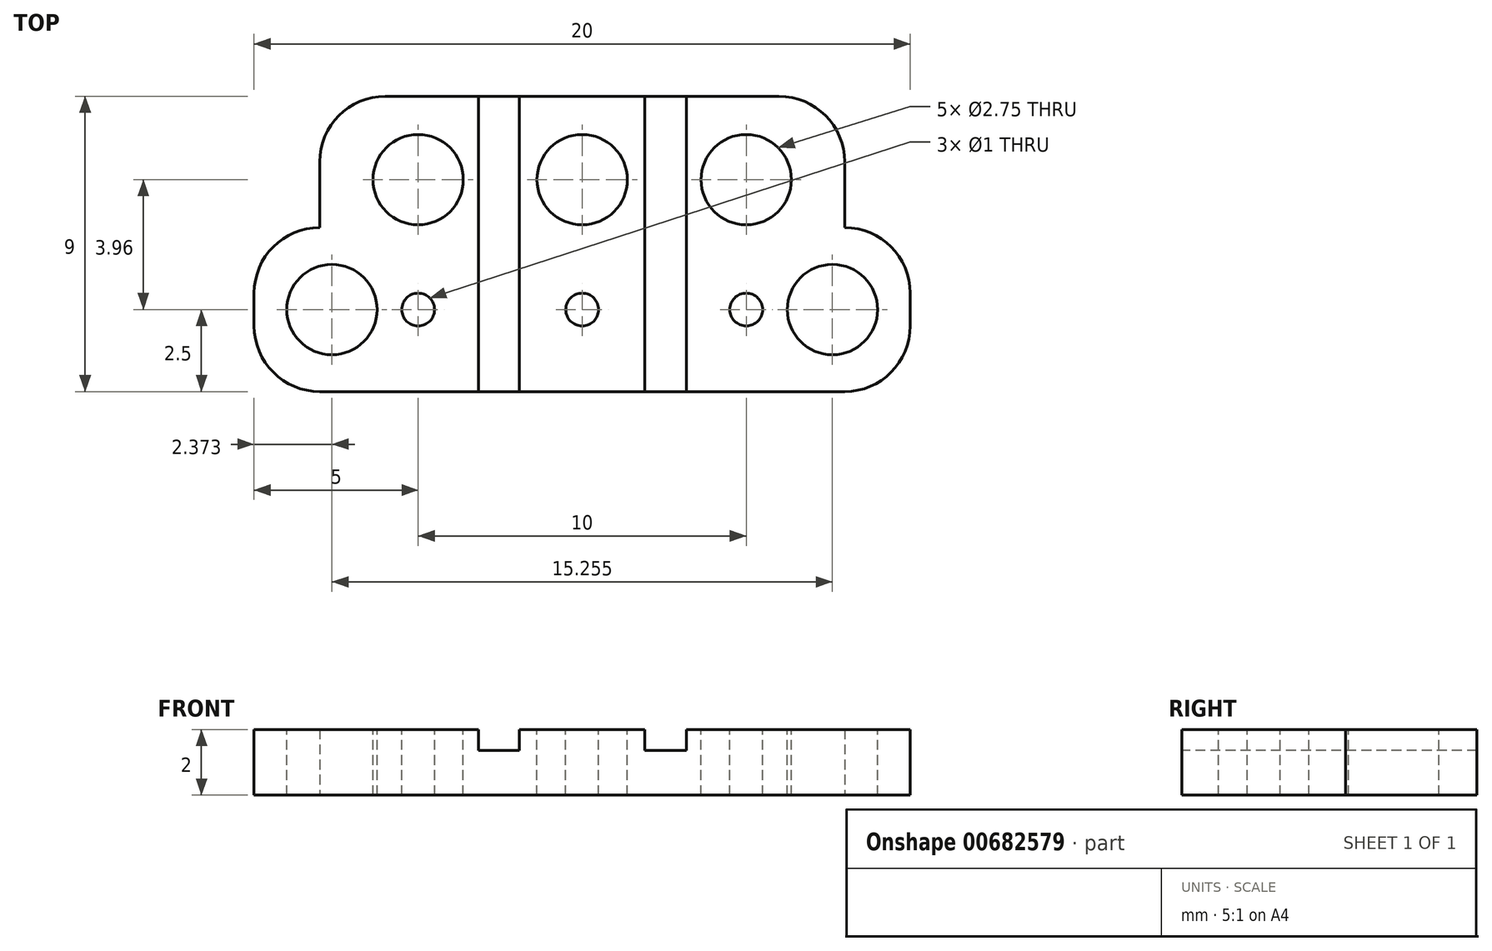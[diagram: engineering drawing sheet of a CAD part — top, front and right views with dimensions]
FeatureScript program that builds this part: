
annotation { "Feature Type Name" : "Feature", "Feature Type Description" : "" }
export const myFeature = defineFeature(function(context is Context, id is Id, definition is map)
    precondition{}
    {
        {
            var Q0;
            Q0=qCreatedBy(makeId("Top.planeOp"),FACE);
            var sketch = newSketch(context, id + "F0", { "sketchPlane" : qUnion([Q0])});
            skLineSegment(sketch, "E0.bottom", {"start": v(10, -2.5) * mm, "end": v(-10, -2.5) * mm});
            skLineSegment(sketch, "E0.top", {"start": v(10, 2.5) * mm, "end": v(-10, 2.5) * mm});
            skLineSegment(sketch, "E0.left", {"start": v(10, -2.5) * mm, "end": v(10, 2.5) * mm});
            skLineSegment(sketch, "E0.right", {"start": v(-10, -2.5) * mm, "end": v(-10, 2.5) * mm});
            skPoint(sketch, "E0.middle", {"position": v(0, 0) * mm});
            skSolve(sketch);
        }
        {
            var Q0;
            Q0 = qSketchRegion(id + "F0", true);
            extrude(context, id + "F1", {"entities" : qUnion([Q0]), "depth" : 2 * mm, "offsetDistance" : 25.4 * mm});
        }
        {
            var Q0;
            Q0=makeQuery(id+"F1.opExtrude","SWEPT_EDGE",EDGE,{"disambiguationData":[OSD([sQuery(id+"F0.wireOp",EDGE,"E0.bottom"),sQuery(id+"F0.wireOp",EDGE,"E0.right")])]});
            var Q1;
            Q1=makeQuery(id+"F1.opExtrude","SWEPT_EDGE",EDGE,{"disambiguationData":[OSD([sQuery(id+"F0.wireOp",EDGE,"E0.top"),sQuery(id+"F0.wireOp",EDGE,"E0.right")])]});
            var Q2;
            Q2=makeQuery(id+"F1.opExtrude","SWEPT_EDGE",EDGE,{"disambiguationData":[OSD([sQuery(id+"F0.wireOp",EDGE,"E0.top"),sQuery(id+"F0.wireOp",EDGE,"E0.left")])]});
            var Q3;
            Q3=makeQuery(id+"F1.opExtrude","SWEPT_EDGE",EDGE,{"disambiguationData":[OSD([sQuery(id+"F0.wireOp",EDGE,"E0.bottom"),sQuery(id+"F0.wireOp",EDGE,"E0.left")])]});
            fillet(context, id + "F2", {"entities" : qUnion([Q0, Q1, Q2, Q3]), "radius" : 2 * mm, "tangentPropagation" : true, "allowEdgeOverflow" : false});
        }
        {
            var Q0;
            Q0=makeQuery(id+"F1.opExtrude","SWEPT_FACE",FACE,{"disambiguationData":[OSD([sQuery(id+"F0.wireOp",EDGE,"E0.top")])]});
            var sketch = newSketch(context, id + "F3", { "sketchPlane" : qUnion([Q0])});
            skLineSegment(sketch, "E1.bottom", {"start": v(-8, 2) * mm, "end": v(8, 2) * mm});
            skLineSegment(sketch, "E1.top", {"start": v(-8, 0) * mm, "end": v(8, 0) * mm});
            skLineSegment(sketch, "E1.left", {"start": v(-8, 2) * mm, "end": v(-8, 0) * mm});
            skLineSegment(sketch, "E1.right", {"start": v(8, 2) * mm, "end": v(8, 0) * mm});
            skSolve(sketch);
        }
        {
            var Q0;
            Q0=makeQuery(id+"F3.imprint","IMPRINT",FACE,{"disambiguationData":[TD([[makeQuery(id+"F3.imprint","IMPRINT",EDGE,{"derivedFrom":sQuery(id+"F3.wireOp",EDGE,"E1.bottom")}),-1.0]])]});
            extrude(context, id + "F4", {"entities" : qUnion([Q0]), "operationType" : NewBodyOperationType.ADD, "depth" : 4 * mm, "offsetDistance" : 25.4 * mm});
        }
        {
            var Q0;
            Q0=makeQuery(id+"F4.opExtrude","CAP_EDGE",EDGE,{"disambiguationData":[OSD([sQuery(id+"F3.wireOp",EDGE,"E1.right")])],"isStart":false});
            var Q1;
            Q1=makeQuery(id+"F4.opExtrude","CAP_EDGE",EDGE,{"disambiguationData":[OSD([sQuery(id+"F3.wireOp",EDGE,"E1.left")])],"isStart":false});
            fillet(context, id + "F5", {"entities" : qUnion([Q0, Q1]), "radius" : 2 * mm, "tangentPropagation" : true, "allowEdgeOverflow" : false});
        }
        {
            var Q0;
            Q0=makeQuery(id+"F4.boolean.opBoolean","MERGE",FACE,{"derivedFrom":[makeQuery(id+"F1.opExtrude","CAP_FACE",FACE,{"disambiguationData":[OSD([sQuery(id+"F0.wireOp",EDGE,"E0.bottom"),sQuery(id+"F0.wireOp",EDGE,"E0.top"),sQuery(id+"F0.wireOp",EDGE,"E0.left"),sQuery(id+"F0.wireOp",EDGE,"E0.right")])],"isStart":false}),makeQuery(id+"F4.opExtrude","SWEPT_FACE",FACE,{"disambiguationData":[OSD([sQuery(id+"F3.wireOp",EDGE,"E1.bottom")])]})]});
            var sketch = newSketch(context, id + "F6", { "sketchPlane" : qUnion([Q0])});
            skCircle(sketch, "E2", {"center": v(0, 0) * mm, "radius": 0.5 * mm});
            skCircle(sketch, "E3", {"center": v(5, 0) * mm, "radius": 0.5 * mm});
            skCircle(sketch, "E4", {"center": v(-5, 0) * mm, "radius": 0.5 * mm});
            skSolve(sketch);
        }
        {
            var Q0;
            Q0=makeQuery(id+"F6.imprint","IMPRINT",FACE,{"disambiguationData":[TD([[makeQuery(id+"F6.imprint","IMPRINT",EDGE,{"derivedFrom":sQuery(id+"F6.wireOp",EDGE,"E2")}),1.0]])]});
            var Q1;
            Q1=makeQuery(id+"F6.imprint","IMPRINT",FACE,{"disambiguationData":[TD([[makeQuery(id+"F6.imprint","IMPRINT",EDGE,{"derivedFrom":sQuery(id+"F6.wireOp",EDGE,"E4")}),1.0]])]});
            var Q2;
            Q2=makeQuery(id+"F6.imprint","IMPRINT",FACE,{"disambiguationData":[TD([[makeQuery(id+"F6.imprint","IMPRINT",EDGE,{"derivedFrom":sQuery(id+"F6.wireOp",EDGE,"E3")}),1.0]])]});
            extrude(context, id + "F7", {"entities" : qUnion([Q0, Q1, Q2]), "operationType" : NewBodyOperationType.REMOVE, "endBound" : BoundingType.THROUGH_ALL, "oppositeDirection" : true, "depth" : 25.4 * mm, "offsetDistance" : 25.4 * mm});
        }
        {
            var Q0;
            Q0=makeQuery(id+"F4.boolean.opBoolean","MERGE",FACE,{"derivedFrom":[makeQuery(id+"F1.opExtrude","CAP_FACE",FACE,{"disambiguationData":[OSD([sQuery(id+"F0.wireOp",EDGE,"E0.bottom"),sQuery(id+"F0.wireOp",EDGE,"E0.top"),sQuery(id+"F0.wireOp",EDGE,"E0.left"),sQuery(id+"F0.wireOp",EDGE,"E0.right")])],"isStart":false}),makeQuery(id+"F4.opExtrude","SWEPT_FACE",FACE,{"disambiguationData":[OSD([sQuery(id+"F3.wireOp",EDGE,"E1.bottom")])]})]});
            var sketch = newSketch(context, id + "F8", { "sketchPlane" : qUnion([Q0])});
            skCircle(sketch, "E5", {"center": v(-7.63, 0) * mm, "radius": 1.38 * mm});
            skCircle(sketch, "E6", {"center": v(7.63, 0) * mm, "radius": 1.38 * mm});
            skCircle(sketch, "E7", {"center": v(-5, 3.96) * mm, "radius": 1.38 * mm});
            skCircle(sketch, "E8", {"center": v(0, 3.96) * mm, "radius": 1.38 * mm});
            skCircle(sketch, "E9", {"center": v(5, 3.96) * mm, "radius": 1.38 * mm});
            skSolve(sketch);
        }
        {
            var Q0;
            Q0 = qSketchRegion(id + "F8", true);
            extrude(context, id + "F9", {"entities" : qUnion([Q0]), "operationType" : NewBodyOperationType.REMOVE, "endBound" : BoundingType.THROUGH_ALL, "oppositeDirection" : true, "depth" : 25.4 * mm, "offsetDistance" : 25.4 * mm});
        }
        {
            var Q0;
            Q0=makeQuery(id+"F4.boolean.opBoolean","MERGE",FACE,{"derivedFrom":[makeQuery(id+"F1.opExtrude","CAP_FACE",FACE,{"disambiguationData":[OSD([sQuery(id+"F0.wireOp",EDGE,"E0.bottom"),sQuery(id+"F0.wireOp",EDGE,"E0.top"),sQuery(id+"F0.wireOp",EDGE,"E0.left"),sQuery(id+"F0.wireOp",EDGE,"E0.right")])],"isStart":false}),makeQuery(id+"F4.opExtrude","SWEPT_FACE",FACE,{"disambiguationData":[OSD([sQuery(id+"F3.wireOp",EDGE,"E1.bottom")])]})]});
            var sketch = newSketch(context, id + "F10", { "sketchPlane" : qUnion([Q0])});
            skLineSegment(sketch, "E10.bottom", {"start": v(-3.18, 6.5) * mm, "end": v(-1.9, 6.5) * mm});
            skLineSegment(sketch, "E10.top", {"start": v(-3.18, -2.5) * mm, "end": v(-1.9, -2.5) * mm});
            skLineSegment(sketch, "E10.left", {"start": v(-3.18, 6.5) * mm, "end": v(-3.18, -2.5) * mm});
            skLineSegment(sketch, "E10.right", {"start": v(-1.9, 6.5) * mm, "end": v(-1.9, -2.5) * mm});
            skLineSegment(sketch, "E11.bottom", {"start": v(1.9, 6.5) * mm, "end": v(3.17, 6.5) * mm});
            skLineSegment(sketch, "E11.top", {"start": v(1.9, -2.5) * mm, "end": v(3.18, -2.5) * mm});
            skLineSegment(sketch, "E11.left", {"start": v(1.9, 6.5) * mm, "end": v(1.9, -2.5) * mm});
            skLineSegment(sketch, "E11.right", {"start": v(3.17, 6.5) * mm, "end": v(3.18, -2.5) * mm});
            skSolve(sketch);
        }
        {
            var Q0;
            Q0=makeQuery(id+"F4.boolean.opBoolean","MERGE",FACE,{"derivedFrom":[makeQuery(id+"F1.opExtrude","CAP_FACE",FACE,{"disambiguationData":[OSD([sQuery(id+"F0.wireOp",EDGE,"E0.bottom"),sQuery(id+"F0.wireOp",EDGE,"E0.top"),sQuery(id+"F0.wireOp",EDGE,"E0.left"),sQuery(id+"F0.wireOp",EDGE,"E0.right")])],"isStart":false}),makeQuery(id+"F4.opExtrude","SWEPT_FACE",FACE,{"disambiguationData":[OSD([sQuery(id+"F3.wireOp",EDGE,"E1.bottom")])]})]});
            var sketch = newSketch(context, id + "F11", { "sketchPlane" : qUnion([Q0])});
            skLineSegment(sketch, "E12.bottom", {"start": v(-3.16, 6.5) * mm, "end": v(-1.92, 6.5) * mm});
            skLineSegment(sketch, "E12.top", {"start": v(-3.16, -2.5) * mm, "end": v(-1.92, -2.5) * mm});
            skLineSegment(sketch, "E12.left", {"start": v(-3.16, 6.5) * mm, "end": v(-3.16, -2.5) * mm});
            skLineSegment(sketch, "E12.right", {"start": v(-1.92, 6.5) * mm, "end": v(-1.92, -2.5) * mm});
            skLineSegment(sketch, "E13.bottom", {"start": v(1.31, 6.5) * mm, "end": v(3.01, 6.5) * mm});
            skLineSegment(sketch, "E13.top", {"start": v(1.31, -2.5) * mm, "end": v(3.01, -2.5) * mm});
            skLineSegment(sketch, "E13.left", {"start": v(1.31, 6.5) * mm, "end": v(1.31, -2.5) * mm});
            skLineSegment(sketch, "E13.right", {"start": v(3.01, 6.5) * mm, "end": v(3.01, -2.5) * mm});
            skSolve(sketch);
        }
        {
            var Q0;
            Q0=makeQuery(id+"F11.imprint","IMPRINT",FACE,{"disambiguationData":[TD([[makeQuery(id+"F11.imprint","IMPRINT",EDGE,{"derivedFrom":sQuery(id+"F11.wireOp",EDGE,"E12.bottom")}),1.0]])]});
            var Q1;
            Q1=makeQuery(id+"F10.imprint","IMPRINT",FACE,{"disambiguationData":[TD([[makeQuery(id+"F10.imprint","IMPRINT",EDGE,{"derivedFrom":sQuery(id+"F10.wireOp",EDGE,"E11.bottom")}),1.0]])]});
            extrude(context, id + "F12", {"entities" : qUnion([Q0, Q1]), "operationType" : NewBodyOperationType.REMOVE, "oppositeDirection" : true, "depth" : 0.64 * mm, "offsetDistance" : 25.4 * mm});
        }
    });
